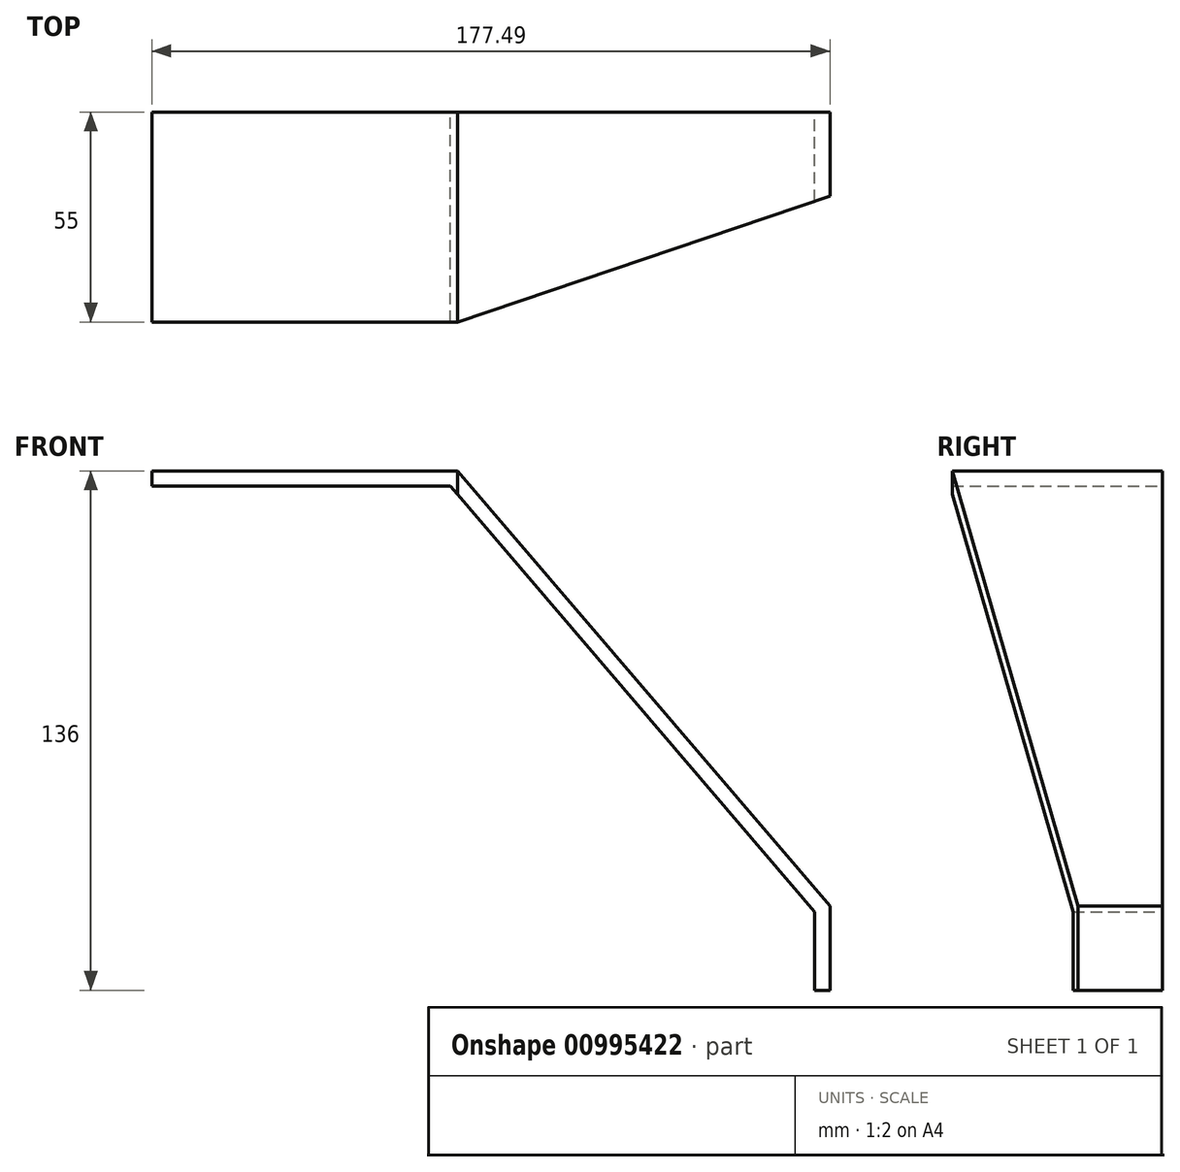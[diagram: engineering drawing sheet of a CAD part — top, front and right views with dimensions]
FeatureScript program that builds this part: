
annotation { "Feature Type Name" : "Feature", "Feature Type Description" : "" }
export const myFeature = defineFeature(function(context is Context, id is Id, definition is map)
    precondition{}
    {
        {
            var Q0;
            Q0=qCreatedBy(makeId("Front.planeOp"),FACE);
            var sketch = newSketch(context, id + "F0", { "sketchPlane" : qUnion([Q0])});
            skLineSegment(sketch, "E0", {"start": v(0, 0) * mm, "end": v(80, 0) * mm});
            skLineSegment(sketch, "E1", {"start": v(80, 0) * mm, "end": v(177.49, -114) * mm});
            skLineSegment(sketch, "E2", {"start": v(177.49, -114) * mm, "end": v(177.49, -136) * mm});
            skLineSegment(sketch, "E3", {"start": v(177.49, -125) * mm, "end": v(0, -125) * mm, "construction": true});
            skLineSegment(sketch, "E4", {"start": v(80, 0) * mm, "end": v(80, -125) * mm, "construction": true});
            skLineSegment(sketch, "E5.0", {"start": v(78.16, -4) * mm, "end": v(173.49, -115.48) * mm});
            skLineSegment(sketch, "E5.1", {"start": v(0, -4) * mm, "end": v(78.16, -4) * mm});
            skLineSegment(sketch, "E6", {"start": v(0, 0) * mm, "end": v(0, -4) * mm});
            skLineSegment(sketch, "E7.0", {"start": v(173.49, -115.48) * mm, "end": v(173.49, -136) * mm});
            skLineSegment(sketch, "E8", {"start": v(173.49, -136) * mm, "end": v(177.49, -136) * mm});
            skSolve(sketch);
        }
        {
            var Q0;
            Q0 = qSketchRegion(id + "F0", true);
            extrude(context, id + "F1", {"entities" : qUnion([Q0]), "depth" : 55 * mm, "offsetDistance" : 25 * mm});
        }
        {
            var Q0;
            Q0=qCreatedBy(makeId("Top.planeOp"),FACE);
            var sketch = newSketch(context, id + "F2", { "sketchPlane" : qUnion([Q0])});
            skPoint(sketch, "E9.0", {"position": v(80, -27.5) * mm});
            skLineSegment(sketch, "E10", {"start": v(80, -55) * mm, "end": v(177.49, -22) * mm});
            skPoint(sketch, "E11.orphan", {"position": v(177.49, -55) * mm});
            skLineSegment(sketch, "E12", {"start": v(80, -55) * mm, "end": v(177.49, -55) * mm});
            skLineSegment(sketch, "E13", {"start": v(177.49, -55) * mm, "end": v(177.49, -22) * mm});
            skPoint(sketch, "E14.0.start.orphan", {"position": v(80, 0) * mm});
            skPoint(sketch, "E15.0.end.orphan", {"position": v(177.49, 0) * mm});
            skSolve(sketch);
        }
        {
            var Q0;
            Q0 = qSketchRegion(id + "F2", true);
            extrude(context, id + "F3", {"entities" : qUnion([Q0]), "operationType" : NewBodyOperationType.REMOVE, "oppositeDirection" : true, "depth" : 150 * mm, "offsetDistance" : 25 * mm});
        }
    });
